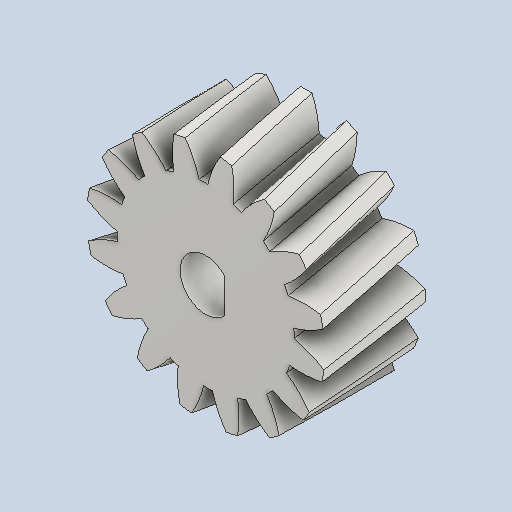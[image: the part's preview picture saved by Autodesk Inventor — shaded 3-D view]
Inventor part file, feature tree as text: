
AUTODESK INVENTOR PART (.ipt)
format: ipt  version: 2023.2 (Build 272271030, 271C)  size: 371,200 bytes
history: native  units: mm (DEFAULTED — no unit token found)
features: plane x3, other x3, sketch x3, extrude x2
ambient origin geometry x8: Origin, YZ Plane, XZ Plane, XY Plane, X Axis, Y Axis, Z Axis, Center Point
bodies: Solid1 (feature_tree)
feature tree (11):
  extrude  "Extrusion1"  Depth=10.0mm TaperAngle=0.0deg
  plane  "Work Plane1"
  plane  "Work Plane2"
  plane  "Work Plane3"
  other  "Spur Gear"
  extrude  "Extrusion2"  Depth=76.2mm TaperAngle=0.0deg
  sketch  "Sketch1"  dims[d0=23.681469mm d1=10.0mm d2=0.0mm]
  sketch  "Sketch2"  dims[d3=20.633469mm d4=76.2mm d5=0.0mm]
  other  "Srf1"
  sketch  "Sketch3"  dims[d6=0.0mm d7=1.963495mm d9=0.0mm d14=0.0mm d15=42.556529mm d16=0.0mm d17=0.0mm d18=0.0mm d19=42.556529mm d20=5.1mm d21=25.4mm d22=0.0mm d24=1.9mm]
  other  "Pitch Diameter"
